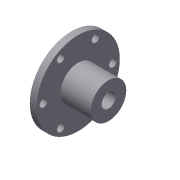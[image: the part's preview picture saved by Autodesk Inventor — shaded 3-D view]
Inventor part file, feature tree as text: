
AUTODESK INVENTOR PART (.ipt)
format: ipt  version: 2011 (Build 150239000, 239)  size: 145,920 bytes
history: native  units: in
note: dims shown in document units (in); Inventor stores cm internally (conversion verified against a paired STEP export)
features: extrude x2, sketch x2, imported_body x1
ambient origin geometry x8: Origin, YZ Plane, XZ Plane, XY Plane, X Axis, Y Axis, Z Axis, Center Point
feature tree (5):
  imported_body  "Base1"
  extrude  "Extrusion1"  Depth=0.375in
  extrude  "Extrusion2"  Depth=0.125in
  sketch  "Sketch1"  dims[d0=1.0in d1=0.0in d2=0.375in]
  sketch  "Sketch2"  dims[d3=0.125in d4=0.125in d5=0.0625in d6=0.0625in d7=1.0in d8=0.0in]
